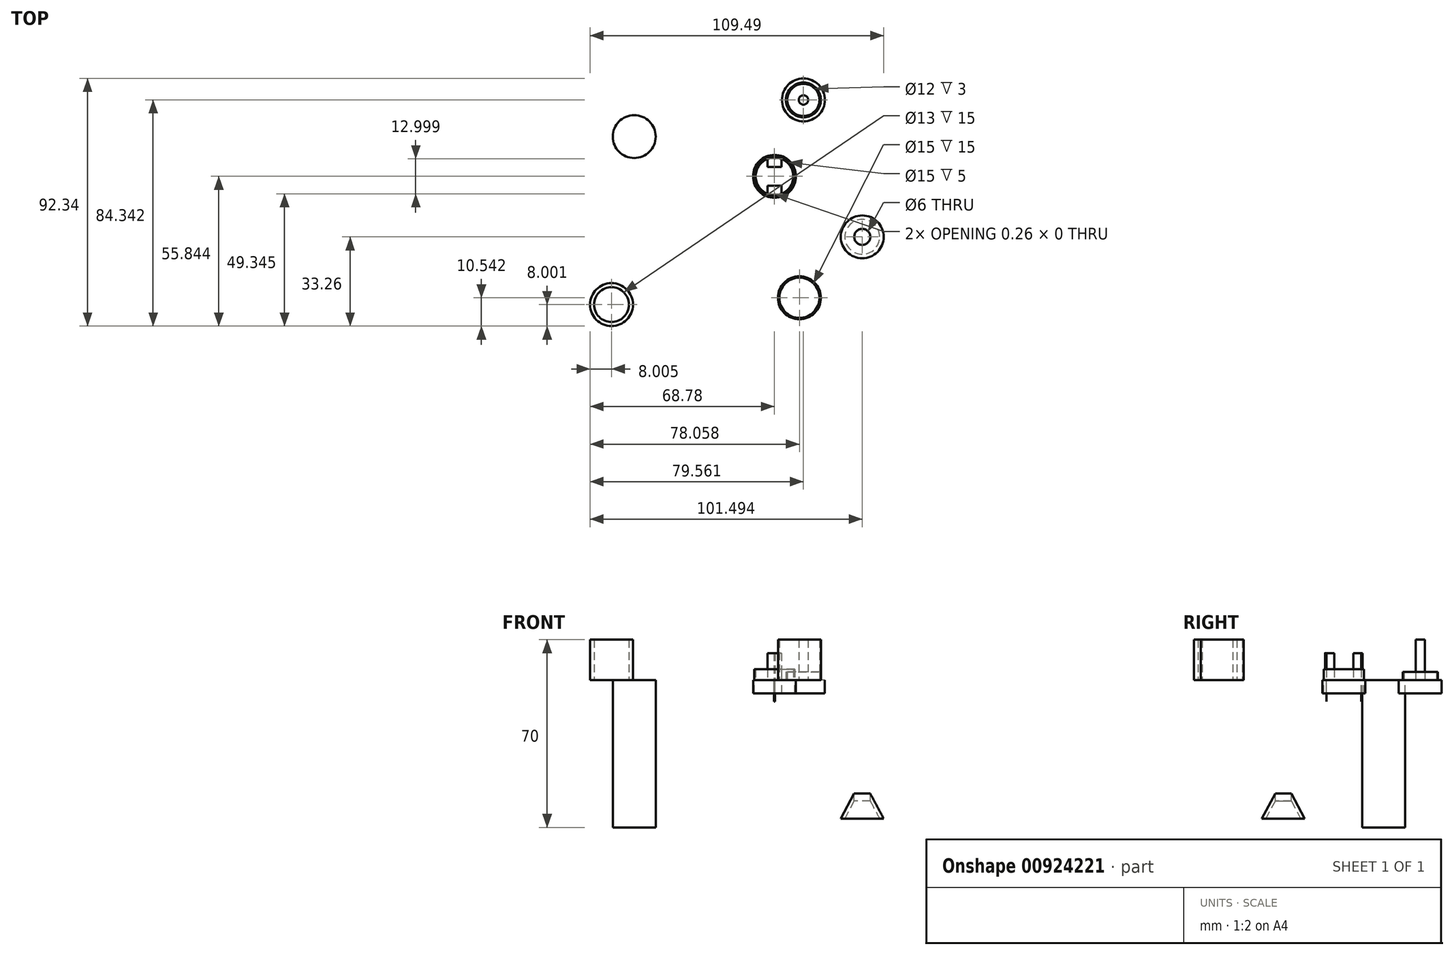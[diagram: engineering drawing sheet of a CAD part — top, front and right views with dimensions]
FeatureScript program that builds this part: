
annotation { "Feature Type Name" : "Feature", "Feature Type Description" : "" }
export const myFeature = defineFeature(function(context is Context, id is Id, definition is map)
    precondition{}
    {
        {
            var Q0;
            Q0=qCreatedBy(makeId("Top.planeOp"),FACE);
            var sketch = newSketch(context, id + "F0", { "sketchPlane" : qUnion([Q0])});
            skCircle(sketch, "E0", {"center": v(-40.85, 37.4) * mm, "radius": 8 * mm});
            skSolve(sketch);
        }
        {
            var Q0;
            Q0 = qSketchRegion(id + "F0", true);
            extrude(context, id + "F1", {"entities" : qUnion([Q0]), "oppositeDirection" : true, "depth" : 55 * mm, "offsetDistance" : 25.4 * mm});
        }
        {
            var Q0;
            Q0=qCreatedBy(makeId("Top.planeOp"),FACE);
            var sketch = newSketch(context, id + "F2", { "sketchPlane" : qUnion([Q0])});
            skCircle(sketch, "E1", {"center": v(22.24, 51.08) * mm, "radius": 8 * mm});
            skCircle(sketch, "E2.0", {"center": v(22.24, 51.08) * mm, "radius": 6.5 * mm});
            skCircle(sketch, "E3.0", {"center": v(22.24, 51.08) * mm, "radius": 6 * mm});
            skCircle(sketch, "E4", {"center": v(22.24, 51.08) * mm, "radius": 1.75 * mm});
            skSolve(sketch);
        }
        {
            var Q0;
            Q0=makeQuery(id+"F2.imprint","IMPRINT",FACE,{"disambiguationData":[TD([[makeQuery(id+"F2.imprint","IMPRINT",EDGE,{"derivedFrom":sQuery(id+"F2.wireOp",EDGE,"E1")}),1.0]])]});
            var Q1;
            Q1=makeQuery(id+"F2.imprint","IMPRINT",FACE,{"disambiguationData":[TD([[makeQuery(id+"F2.imprint","IMPRINT",EDGE,{"derivedFrom":sQuery(id+"F2.wireOp",EDGE,"E3.0")}),1.0]])]});
            var Q2;
            Q2=makeQuery(id+"F2.imprint","IMPRINT",FACE,{"disambiguationData":[TD([[makeQuery(id+"F2.imprint","IMPRINT",EDGE,{"derivedFrom":sQuery(id+"F2.wireOp",EDGE,"E2.0")}),1.0]])]});
            var Q3;
            Q3=makeQuery(id+"F2.imprint","IMPRINT",FACE,{"disambiguationData":[TD([[makeQuery(id+"F2.imprint","IMPRINT",EDGE,{"derivedFrom":sQuery(id+"F2.wireOp",EDGE,"E4")}),1.0]])]});
            var Q4;
            Q4=sQuery(id+"F2.wireOp",EDGE,"E1");
            extrude(context, id + "F3", {"entities" : qUnion([Q0, Q1, Q2, Q3]), "surfaceEntities" : qUnion([Q4]), "oppositeDirection" : true, "depth" : 5 * mm, "offsetDistance" : 25 * mm});
        }
        {
            var Q0;
            Q0=makeQuery(id+"F2.imprint","IMPRINT",FACE,{"disambiguationData":[TD([[makeQuery(id+"F2.imprint","IMPRINT",EDGE,{"derivedFrom":sQuery(id+"F2.wireOp",EDGE,"E2.0")}),1.0]])]});
            extrude(context, id + "F4", {"entities" : qUnion([Q0]), "operationType" : NewBodyOperationType.ADD, "depth" : 3 * mm, "offsetDistance" : 25 * mm});
        }
        {
            var Q0;
            Q0=makeQuery(id+"F2.imprint","IMPRINT",FACE,{"disambiguationData":[TD([[makeQuery(id+"F2.imprint","IMPRINT",EDGE,{"derivedFrom":sQuery(id+"F2.wireOp",EDGE,"E4")}),1.0]])]});
            extrude(context, id + "F5", {"entities" : qUnion([Q0]), "operationType" : NewBodyOperationType.ADD, "depth" : 15 * mm, "offsetDistance" : 25 * mm});
        }
        {
            var Q0;
            Q0=qCreatedBy(makeId("Top.planeOp"),FACE);
            var sketch = newSketch(context, id + "F6", { "sketchPlane" : qUnion([Q0])});
            skCircle(sketch, "E5", {"center": v(11.46, 22.58) * mm, "radius": 8 * mm});
            skCircle(sketch, "E6.0", {"center": v(11.46, 22.58) * mm, "radius": 6.5 * mm});
            skCircle(sketch, "E7.0", {"center": v(11.46, 22.58) * mm, "radius": 6 * mm});
            skPoint(sketch, "E8.orphan", {"position": v(8.34, 28.29) * mm});
            skPoint(sketch, "E9.orphan", {"position": v(14.58, 28.29) * mm});
            skPoint(sketch, "E10.orphan", {"position": v(14.58, 16.88) * mm});
            skPoint(sketch, "E11.orphan", {"position": v(8.34, 16.88) * mm});
            skPoint(sketch, "E12", {"position": v(7.96, 22.58) * mm});
            skPoint(sketch, "E13", {"position": v(14.96, 22.58) * mm});
            skPoint(sketch, "E14", {"position": v(7.46, 22.58) * mm});
            skPoint(sketch, "E15", {"position": v(15.46, 22.58) * mm});
            skCircle(sketch, "E16.0", {"center": v(11.46, 22.58) * mm, "radius": 7.5 * mm});
            skCircle(sketch, "E17.0", {"center": v(11.46, 22.58) * mm, "radius": 7 * mm});
            skPoint(sketch, "E18.left.end.orphan", {"position": v(8.34, 25.79) * mm});
            skPoint(sketch, "E19.start.orphan", {"position": v(8.34, 19.38) * mm});
            skLineSegment(sketch, "E20.bottom", {"start": v(11.33, 29.08) * mm, "end": v(11.59, 29.08) * mm});
            skLineSegment(sketch, "E20.top", {"start": v(11.33, 16.09) * mm, "end": v(11.59, 16.09) * mm});
            skLineSegment(sketch, "E20.left", {"start": v(8.86, 29.08) * mm, "end": v(8.86, 26.08) * mm});
            skLineSegment(sketch, "E20.right", {"start": v(14.06, 29.08) * mm, "end": v(14.06, 26.08) * mm});
            skPoint(sketch, "E21", {"position": v(8.86, 26.08) * mm});
            skPoint(sketch, "E22", {"position": v(8.86, 19.09) * mm});
            skLineSegment(sketch, "E23", {"start": v(8.86, 19.09) * mm, "end": v(14.06, 19.09) * mm});
            skLineSegment(sketch, "E24", {"start": v(8.86, 26.08) * mm, "end": v(14.06, 26.08) * mm});
            skLineSegment(sketch, "E25.trimOffspring", {"start": v(8.86, 19.09) * mm, "end": v(8.86, 16.09) * mm});
            skLineSegment(sketch, "E26.trimOffspring", {"start": v(14.06, 19.09) * mm, "end": v(14.06, 16.09) * mm});
            skSolve(sketch);
        }
        {
            var Q0;
            {var subQ0=sQuery(id+"F6.wireOp",EDGE,"E18.left");Q0=makeQuery(id+"F6.imprint","IMPRINT",FACE,{"disambiguationData":[TD([[makeQuery(id+"F6.imprint","IMPRINT",EDGE,{"derivedFrom":subQ0}),1.0]])]});}
            var Q1;
            {var subQ1=sQuery(id+"F6.wireOp",EDGE,"E18.left");Q1=makeQuery(id+"F6.imprint","IMPRINT",FACE,{"disambiguationData":[TD([[makeQuery(id+"F6.imprint","IMPRINT",EDGE,{"derivedFrom":subQ1}),-1.0]])]});}
            var Q2;
            Q2=makeQuery(id+"F6.imprint","IMPRINT",FACE,{"disambiguationData":[TD([[makeQuery(id+"F6.imprint","IMPRINT",EDGE,{"derivedFrom":sQuery(id+"F6.wireOp",EDGE,"E5")}),1.0]])]});
            var Q3;
            Q3=makeQuery(id+"F6.imprint","IMPRINT",FACE,{"disambiguationData":[TD([[makeQuery(id+"F6.imprint","IMPRINT",EDGE,{"derivedFrom":sQuery(id+"F6.wireOp",EDGE,"E19")}),-1.0]])]});
            var Q4;
            Q4=makeQuery(id+"F6.imprint","IMPRINT",FACE,{"disambiguationData":[TD([[makeQuery(id+"F6.imprint","IMPRINT",EDGE,{"derivedFrom":sQuery(id+"F6.wireOp",EDGE,"E6.0")}),1.0]])]});
            extrude(context, id + "F7", {"entities" : qUnion([Q0, Q1, Q2, Q3, Q4]), "oppositeDirection" : true, "depth" : 5 * mm, "offsetDistance" : 25 * mm});
        }
        {
            var Q0;
            Q0=makeQuery(id+"F6.imprint","IMPRINT",FACE,{"disambiguationData":[TD([[makeQuery(id+"F6.imprint","IMPRINT",EDGE,{"derivedFrom":sQuery(id+"F6.wireOp",EDGE,"E6.0")}),1.0]])]});
            extrude(context, id + "F8", {"entities" : qUnion([Q0]), "operationType" : NewBodyOperationType.ADD, "oppositeDirection" : true, "depth" : 8 * mm, "offsetDistance" : 25 * mm});
        }
        {
            var Q0;
            Q0=qCreatedBy(makeId("Top.planeOp"),FACE);
            var sketch = newSketch(context, id + "F9", { "sketchPlane" : qUnion([Q0])});
            skCircle(sketch, "E27", {"center": v(-49.32, -25.26) * mm, "radius": 8 * mm});
            skCircle(sketch, "E28.0", {"center": v(-49.32, -25.26) * mm, "radius": 6.5 * mm});
            skSolve(sketch);
        }
        {
            var Q0;
            Q0=makeQuery(id+"F9.imprint","IMPRINT",FACE,{"disambiguationData":[TD([[makeQuery(id+"F9.imprint","IMPRINT",EDGE,{"derivedFrom":sQuery(id+"F9.wireOp",EDGE,"E27")}),1.0]])]});
            extrude(context, id + "F10", {"entities" : qUnion([Q0]), "depth" : 15 * mm, "offsetDistance" : 25 * mm});
        }
        {
            var Q0;
            Q0=qCreatedBy(makeId("Top.planeOp"),FACE);
            var sketch = newSketch(context, id + "F11", { "sketchPlane" : qUnion([Q0])});
            skCircle(sketch, "E29", {"center": v(20.74, -22.72) * mm, "radius": 8 * mm});
            skCircle(sketch, "E30.0", {"center": v(20.74, -22.72) * mm, "radius": 6.5 * mm});
            skCircle(sketch, "E31", {"center": v(20.74, -22.72) * mm, "radius": 3 * mm});
            skCircle(sketch, "E32.0", {"center": v(20.74, -22.72) * mm, "radius": 7.5 * mm});
            skSolve(sketch);
        }
        {
            var Q0;
            Q0=qCreatedBy(makeId("Front.planeOp"),FACE);
            var sketch = newSketch(context, id + "F12", { "sketchPlane" : qUnion([Q0])});
            skLineSegment(sketch, "E33.top", {"start": v(36.17, -51.76) * mm, "end": v(37.67, -51.76) * mm});
            skLineSegment(sketch, "E33.right", {"start": v(44.17, -36.76) * mm, "end": v(44.17, -51.76) * mm});
            skLineSegment(sketch, "E34", {"start": v(36.17, -51.76) * mm, "end": v(41.17, -42.39) * mm});
            skPoint(sketch, "E35", {"position": v(37.67, -51.76) * mm});
            skPoint(sketch, "E36", {"position": v(41.17, -51.76) * mm});
            skLineSegment(sketch, "E37", {"start": v(41.17, -45.2) * mm, "end": v(41.17, -42.39) * mm});
            skLineSegment(sketch, "E38", {"start": v(37.67, -51.76) * mm, "end": v(41.17, -45.2) * mm});
            skSolve(sketch);
        }
        {
            var Q0;
            Q0=makeQuery(id+"F12.imprint","IMPRINT",FACE,{"disambiguationData":[TD([[makeQuery(id+"F12.imprint","IMPRINT",EDGE,{"derivedFrom":sQuery(id+"F12.wireOp",EDGE,"E33.top")}),1.0]])]});
            var Q1;
            Q1=sQuery(id+"F12.wireOp",EDGE,"E33.right");
            revolve(context, id + "F13", {"surfaceOperationType" : NewSurfaceOperationType.NEW, "entities" : qUnion([Q0]), "axis" : qUnion([Q1]), "revolveType" : RevolveType.FULL});
        }
        {
            var Q0;
            Q0=makeQuery(id+"F6.imprint","IMPRINT",FACE,{"disambiguationData":[TD([[makeQuery(id+"F6.imprint","IMPRINT",EDGE,{"derivedFrom":sQuery(id+"F6.wireOp",EDGE,"E16.0")}),1.0]])]});
            extrude(context, id + "F14", {"entities" : qUnion([Q0]), "depth" : 4 * mm, "offsetDistance" : 25 * mm});
        }
        {
            var Q0;
            {var subQ0=sQuery(id+"F6.wireOp",EDGE,"E20.top");Q0=makeQuery(id+"F6.imprint","IMPRINT",FACE,{"disambiguationData":[TD([[makeQuery(id+"F6.imprint","IMPRINT",EDGE,{"derivedFrom":subQ0}),1.0]])]});}
            var Q1;
            {var subQ5=sQuery(id+"F6.wireOp",EDGE,"E24");Q1=makeQuery(id+"F6.imprint","IMPRINT",FACE,{"disambiguationData":[TD([[makeQuery(id+"F6.imprint","IMPRINT",EDGE,{"derivedFrom":subQ5}),1.0]])]});}
            var Q2;
            {var subQ5=sQuery(id+"F6.wireOp",EDGE,"E20.bottom");var subQ6=sQuery(id+"F6.wireOp",EDGE,"E6.0");var subQ9=makeQuery(id+"F6.imprint","INTERSECT",VERTEX,{"disambiguationData":[OD(1.0)],"derivedFrom":[subQ6,subQ5]});Q2=makeQuery(id+"F6.imprint","IMPRINT",FACE,{"disambiguationData":[TD([[makeQuery(id+"F6.imprint","IMPRINT",EDGE,{"disambiguationData":[TD([[subQ9,1.0]])],"derivedFrom":subQ6}),-1.0]])]});}
            var Q3;
            {var subQ0=sQuery(id+"F6.wireOp",EDGE,"E20.top");var subQ1=sQuery(id+"F6.wireOp",EDGE,"E6.0");var subQ9=makeQuery(id+"F6.imprint","INTERSECT",VERTEX,{"disambiguationData":[OD(0.0)],"derivedFrom":[subQ1,subQ0]});Q3=makeQuery(id+"F6.imprint","IMPRINT",FACE,{"disambiguationData":[TD([[makeQuery(id+"F6.imprint","IMPRINT",EDGE,{"disambiguationData":[TD([[subQ9,1.0]])],"derivedFrom":subQ1}),-1.0]])]});}
            var Q4;
            {var subQ5=sQuery(id+"F6.wireOp",EDGE,"E23");Q4=makeQuery(id+"F6.imprint","IMPRINT",FACE,{"disambiguationData":[TD([[makeQuery(id+"F6.imprint","IMPRINT",EDGE,{"derivedFrom":subQ5}),-1.0]])]});}
            var Q5;
            {var subQ5=sQuery(id+"F6.wireOp",EDGE,"E20.bottom");Q5=makeQuery(id+"F6.imprint","IMPRINT",FACE,{"disambiguationData":[TD([[makeQuery(id+"F6.imprint","IMPRINT",EDGE,{"derivedFrom":subQ5}),-1.0]])]});}
            extrude(context, id + "F15", {"entities" : qUnion([Q0, Q1, Q2, Q3, Q4, Q5]), "operationType" : NewBodyOperationType.ADD, "depth" : 10 * mm, "offsetDistance" : 25 * mm});
        }
        {
            var Q0;
            Q0=makeQuery(id+"F11.imprint","IMPRINT",FACE,{"disambiguationData":[TD([[makeQuery(id+"F11.imprint","IMPRINT",EDGE,{"derivedFrom":sQuery(id+"F11.wireOp",EDGE,"E29")}),1.0]])]});
            extrude(context, id + "F16", {"entities" : qUnion([Q0]), "depth" : 15 * mm, "offsetDistance" : 25 * mm});
        }
    });
